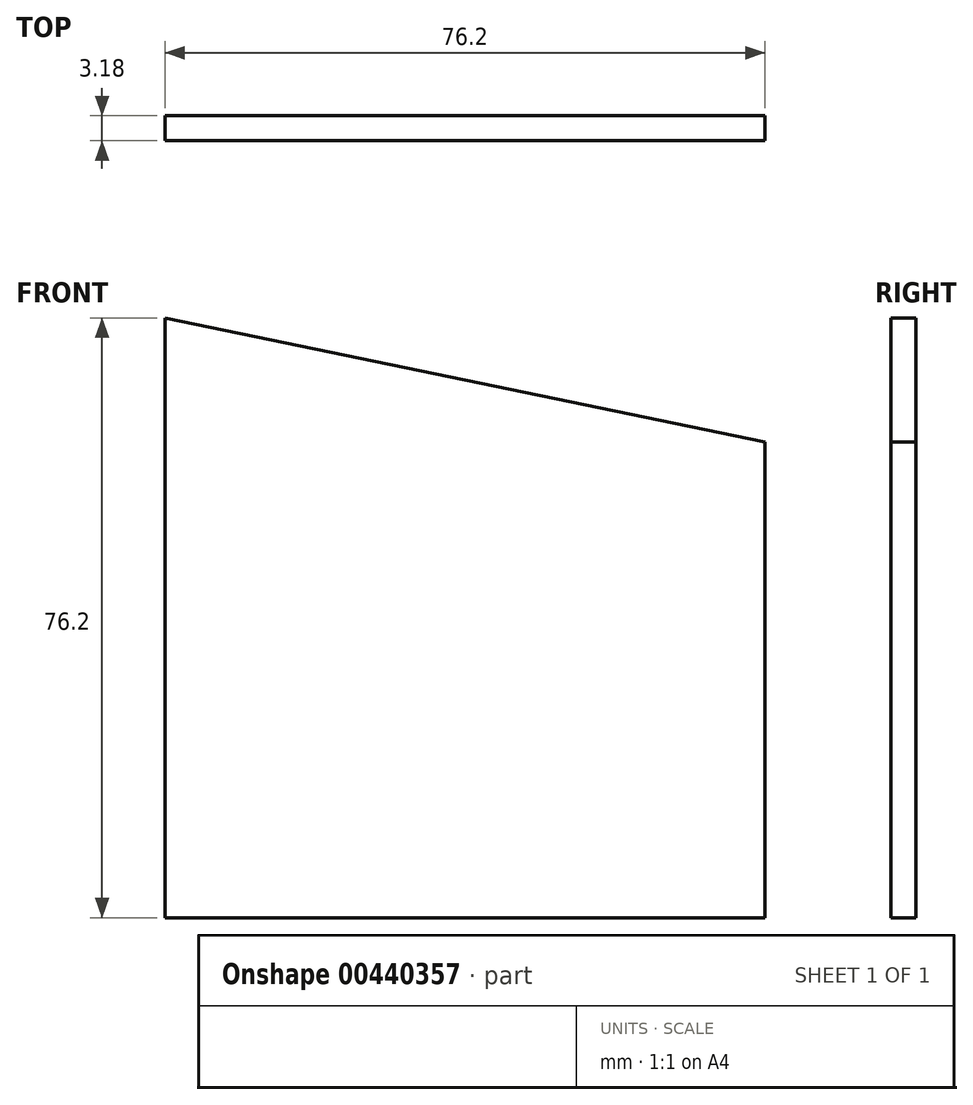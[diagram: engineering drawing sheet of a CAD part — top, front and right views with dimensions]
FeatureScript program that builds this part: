
annotation { "Feature Type Name" : "Feature", "Feature Type Description" : "" }
export const myFeature = defineFeature(function(context is Context, id is Id, definition is map)
    precondition{}
    {
        {
            var Q0;
            Q0=qCreatedBy(makeId("Front.planeOp"),FACE);
            var sketch = newSketch(context, id + "F0", { "sketchPlane" : qUnion([Q0])});
            skLineSegment(sketch, "E0.top", {"start": v(-38.1, -38.1) * mm, "end": v(38.1, -38.1) * mm});
            skLineSegment(sketch, "E0.left", {"start": v(-38.1, 38.1) * mm, "end": v(-38.1, -38.1) * mm});
            skPoint(sketch, "E0.middle", {"position": v(0, 0) * mm});
            skLineSegment(sketch, "E1", {"start": v(38.1, -38.1) * mm, "end": v(38.1, 22.35) * mm});
            skLineSegment(sketch, "E2", {"start": v(38.1, 22.35) * mm, "end": v(-38.1, 38.1) * mm});
            skSolve(sketch);
        }
        {
            var Q0;
            Q0=makeQuery(id+"F0.imprint","IMPRINT",FACE,{"disambiguationData":[TD([[makeQuery(id+"F0.imprint","IMPRINT",EDGE,{"derivedFrom":sQuery(id+"F0.wireOp",EDGE,"E0.top")}),1.0]])]});
            extrude(context, id + "F1", {"entities" : qUnion([Q0]), "endBound" : BoundingType.SYMMETRIC, "depth" : 3.17 * mm});
        }
    });
